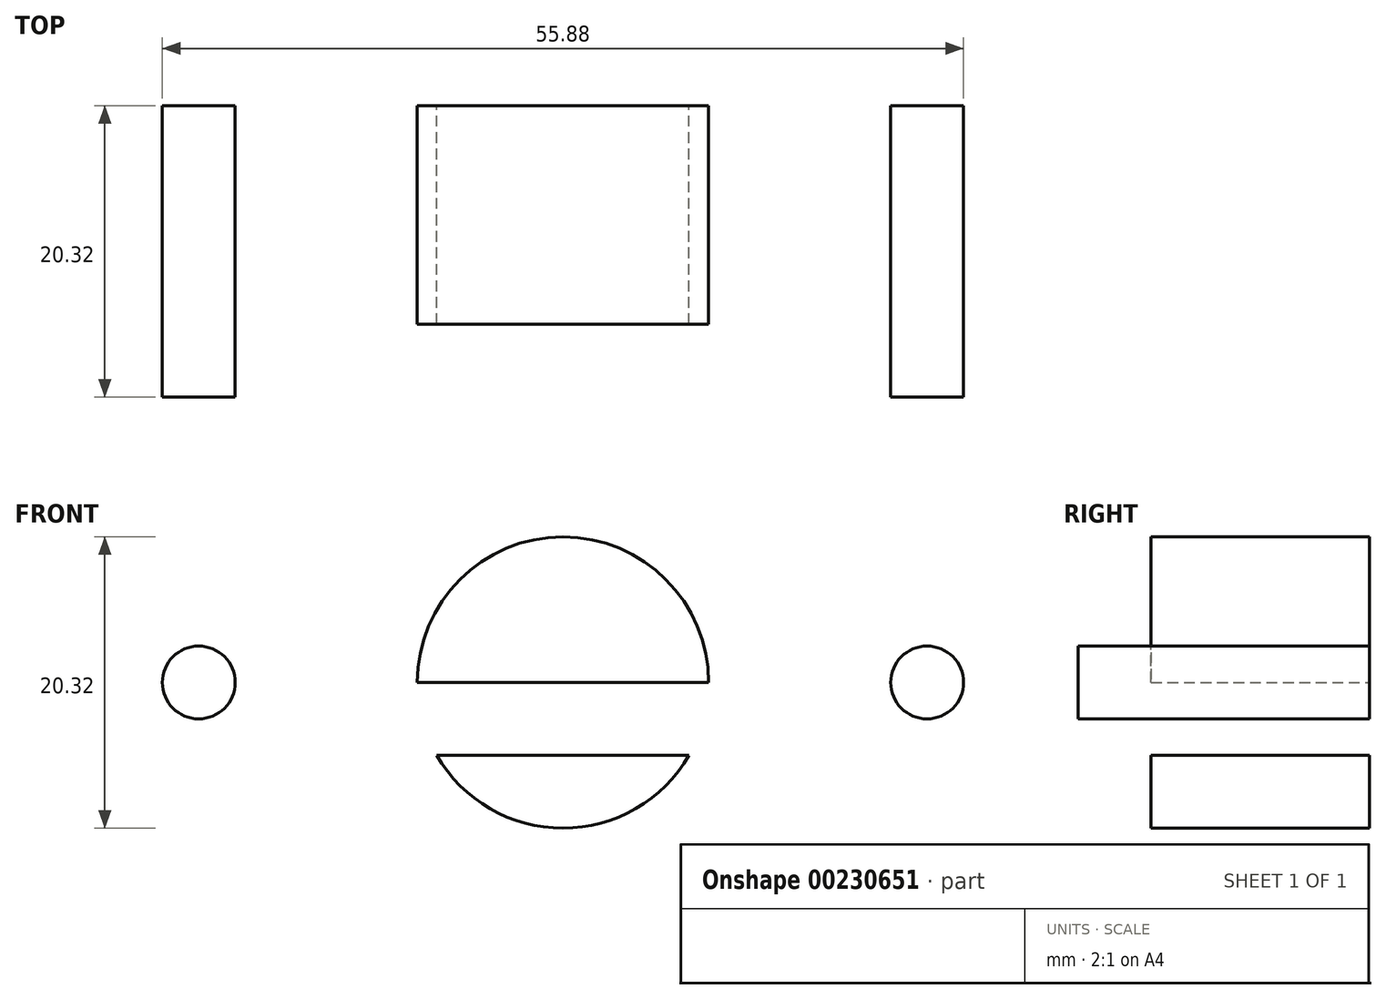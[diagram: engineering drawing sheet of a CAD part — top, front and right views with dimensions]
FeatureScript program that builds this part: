
annotation { "Feature Type Name" : "Feature", "Feature Type Description" : "" }
export const myFeature = defineFeature(function(context is Context, id is Id, definition is map)
    precondition{}
    {
        {
            var Q0;
            Q0=qCreatedBy(makeId("Front.planeOp"),FACE);
            var sketch = newSketch(context, id + "F0", { "sketchPlane" : qUnion([Q0])});
            skCircle(sketch, "E0", {"center": v(0, 0) * mm, "radius": 50.8 * mm, "construction": true});
            skCircle(sketch, "E1", {"center": v(0, 0) * mm, "radius": 10.16 * mm});
            skLineSegment(sketch, "E2", {"start": v(-25.4, 0) * mm, "end": v(25.4, 0) * mm});
            skCircle(sketch, "E3", {"center": v(0, 0) * mm, "radius": 25.4 * mm, "construction": true});
            skArc(sketch, "E4.0.startCap", {"start": v(-25.4, -5.08) * mm, "mid": v(-30.48, 0) * mm, "end": v(-25.4, 5.08) * mm});
            skArc(sketch, "E4.0.endCap", {"start": v(25.4, 5.08) * mm, "mid": v(30.48, 0) * mm, "end": v(25.4, -5.08) * mm});
            skLineSegment(sketch, "E4.0.left", {"start": v(-25.4, 5.08) * mm, "end": v(25.4, 5.08) * mm});
            skLineSegment(sketch, "E4.0.right", {"start": v(-25.4, -5.08) * mm, "end": v(25.4, -5.08) * mm});
            skCircle(sketch, "E5", {"center": v(-25.4, 0) * mm, "radius": 2.54 * mm});
            skCircle(sketch, "E6", {"center": v(25.4, 0) * mm, "radius": 2.54 * mm});
            skSolve(sketch);
        }
        {
            var Q0;
            {var subQ1=sQuery(id+"F0.wireOp",EDGE,"E4.0.startCap");Q0=makeQuery(id+"F0.imprint","IMPRINT",FACE,{"disambiguationData":[TD([[makeQuery(id+"F0.imprint","IMPRINT",EDGE,{"derivedFrom":subQ1}),-1.0]])]});}
            var Q1;
            Q1=makeQuery(id+"F0.imprint","IMPRINT",FACE,{"disambiguationData":[TD([[makeQuery(id+"F0.imprint","IMPRINT",EDGE,{"derivedFrom":sQuery(id+"F0.wireOp",EDGE,"E5")}),1.0]])]});
            var Q2;
            {var subQ0=sQuery(id+"F0.wireOp",EDGE,"E4.0.left");var subQ1=sQuery(id+"F0.wireOp",EDGE,"E1");var subQ2=makeQuery(id+"F0.imprint","INTERSECT",VERTEX,{"disambiguationData":[OD(0.0)],"derivedFrom":[subQ1,subQ0]});Q2=makeQuery(id+"F0.imprint","IMPRINT",FACE,{"disambiguationData":[TD([[makeQuery(id+"F0.imprint","IMPRINT",EDGE,{"disambiguationData":[TD([[subQ2,1.0]])],"derivedFrom":subQ1}),1.0]])]});}
            var Q3;
            {var subQ0=sQuery(id+"F0.wireOp",EDGE,"E2");var subQ1=sQuery(id+"F0.wireOp",EDGE,"E1");var subQ2=makeQuery(id+"F0.imprint","INTERSECT",VERTEX,{"disambiguationData":[OD(1.0)],"derivedFrom":[subQ1,subQ0]});Q3=makeQuery(id+"F0.imprint","IMPRINT",FACE,{"disambiguationData":[TD([[makeQuery(id+"F0.imprint","IMPRINT",EDGE,{"disambiguationData":[TD([[subQ2,-1.0]])],"derivedFrom":subQ1}),1.0]])]});}
            var Q4;
            {var subQ1=sQuery(id+"F0.wireOp",EDGE,"E4.0.endCap");Q4=makeQuery(id+"F0.imprint","IMPRINT",FACE,{"disambiguationData":[TD([[makeQuery(id+"F0.imprint","IMPRINT",EDGE,{"derivedFrom":subQ1}),-1.0]])]});}
            var Q5;
            Q5=makeQuery(id+"F0.imprint","IMPRINT",FACE,{"disambiguationData":[TD([[makeQuery(id+"F0.imprint","IMPRINT",EDGE,{"derivedFrom":sQuery(id+"F0.wireOp",EDGE,"E6")}),1.0]])]});
            var Q6;
            {var subQ0=sQuery(id+"F0.wireOp",EDGE,"E4.0.left");var subQ1=sQuery(id+"F0.wireOp",EDGE,"E1");var subQ2=makeQuery(id+"F0.imprint","INTERSECT",VERTEX,{"disambiguationData":[OD(0.0)],"derivedFrom":[subQ1,subQ0]});Q6=makeQuery(id+"F0.imprint","IMPRINT",FACE,{"disambiguationData":[TD([[makeQuery(id+"F0.imprint","IMPRINT",EDGE,{"disambiguationData":[TD([[subQ2,-1.0]])],"derivedFrom":subQ1}),1.0]])]});}
            var Q7;
            {var subQ0=sQuery(id+"F0.wireOp",EDGE,"E4.0.right");var subQ1=sQuery(id+"F0.wireOp",EDGE,"E1");var subQ2=makeQuery(id+"F0.imprint","INTERSECT",VERTEX,{"disambiguationData":[OD(0.0)],"derivedFrom":[subQ1,subQ0]});Q7=makeQuery(id+"F0.imprint","IMPRINT",FACE,{"disambiguationData":[TD([[makeQuery(id+"F0.imprint","IMPRINT",EDGE,{"disambiguationData":[TD([[subQ2,-1.0]])],"derivedFrom":subQ1}),1.0]])]});}
            extrude(context, id + "F1", {"entities" : qUnion([Q0, Q1, Q2, Q3, Q4, Q5, Q6, Q7]), "depth" : 7.62 * mm});
        }
        {
            var Q0;
            {var subQ0=sQuery(id+"F0.wireOp",EDGE,"E4.0.left");var subQ1=sQuery(id+"F0.wireOp",EDGE,"E1");var subQ2=makeQuery(id+"F0.imprint","INTERSECT",VERTEX,{"disambiguationData":[OD(0.0)],"derivedFrom":[subQ1,subQ0]});Q0=makeQuery(id+"F0.imprint","IMPRINT",FACE,{"disambiguationData":[TD([[makeQuery(id+"F0.imprint","IMPRINT",EDGE,{"disambiguationData":[TD([[subQ2,-1.0]])],"derivedFrom":subQ1}),1.0]])]});}
            var Q1;
            {var subQ0=sQuery(id+"F0.wireOp",EDGE,"E4.0.left");var subQ1=sQuery(id+"F0.wireOp",EDGE,"E1");var subQ2=makeQuery(id+"F0.imprint","INTERSECT",VERTEX,{"disambiguationData":[OD(0.0)],"derivedFrom":[subQ1,subQ0]});Q1=makeQuery(id+"F0.imprint","IMPRINT",FACE,{"disambiguationData":[TD([[makeQuery(id+"F0.imprint","IMPRINT",EDGE,{"disambiguationData":[TD([[subQ2,1.0]])],"derivedFrom":subQ1}),1.0]])]});}
            var Q2;
            {var subQ0=sQuery(id+"F0.wireOp",EDGE,"E2");var subQ1=sQuery(id+"F0.wireOp",EDGE,"E1");var subQ2=makeQuery(id+"F0.imprint","INTERSECT",VERTEX,{"disambiguationData":[OD(1.0)],"derivedFrom":[subQ1,subQ0]});Q2=makeQuery(id+"F0.imprint","IMPRINT",FACE,{"disambiguationData":[TD([[makeQuery(id+"F0.imprint","IMPRINT",EDGE,{"disambiguationData":[TD([[subQ2,-1.0]])],"derivedFrom":subQ1}),1.0]])]});}
            var Q3;
            {var subQ0=sQuery(id+"F0.wireOp",EDGE,"E4.0.right");var subQ1=sQuery(id+"F0.wireOp",EDGE,"E1");var subQ2=makeQuery(id+"F0.imprint","INTERSECT",VERTEX,{"disambiguationData":[OD(0.0)],"derivedFrom":[subQ1,subQ0]});Q3=makeQuery(id+"F0.imprint","IMPRINT",FACE,{"disambiguationData":[TD([[makeQuery(id+"F0.imprint","IMPRINT",EDGE,{"disambiguationData":[TD([[subQ2,-1.0]])],"derivedFrom":subQ1}),1.0]])]});}
            extrude(context, id + "F2", {"entities" : qUnion([Q0, Q1, Q2, Q3]), "operationType" : NewBodyOperationType.ADD, "depth" : 15.24 * mm});
        }
        {
            var Q0;
            Q0=makeQuery(id+"F0.imprint","IMPRINT",FACE,{"disambiguationData":[TD([[makeQuery(id+"F0.imprint","IMPRINT",EDGE,{"derivedFrom":sQuery(id+"F0.wireOp",EDGE,"E5")}),1.0]])]});
            var Q1;
            Q1=makeQuery(id+"F0.imprint","IMPRINT",FACE,{"disambiguationData":[TD([[makeQuery(id+"F0.imprint","IMPRINT",EDGE,{"derivedFrom":sQuery(id+"F0.wireOp",EDGE,"E6")}),1.0]])]});
            extrude(context, id + "F3", {"entities" : qUnion([Q0, Q1]), "operationType" : NewBodyOperationType.ADD, "depth" : 20.32 * mm});
        }
    });
